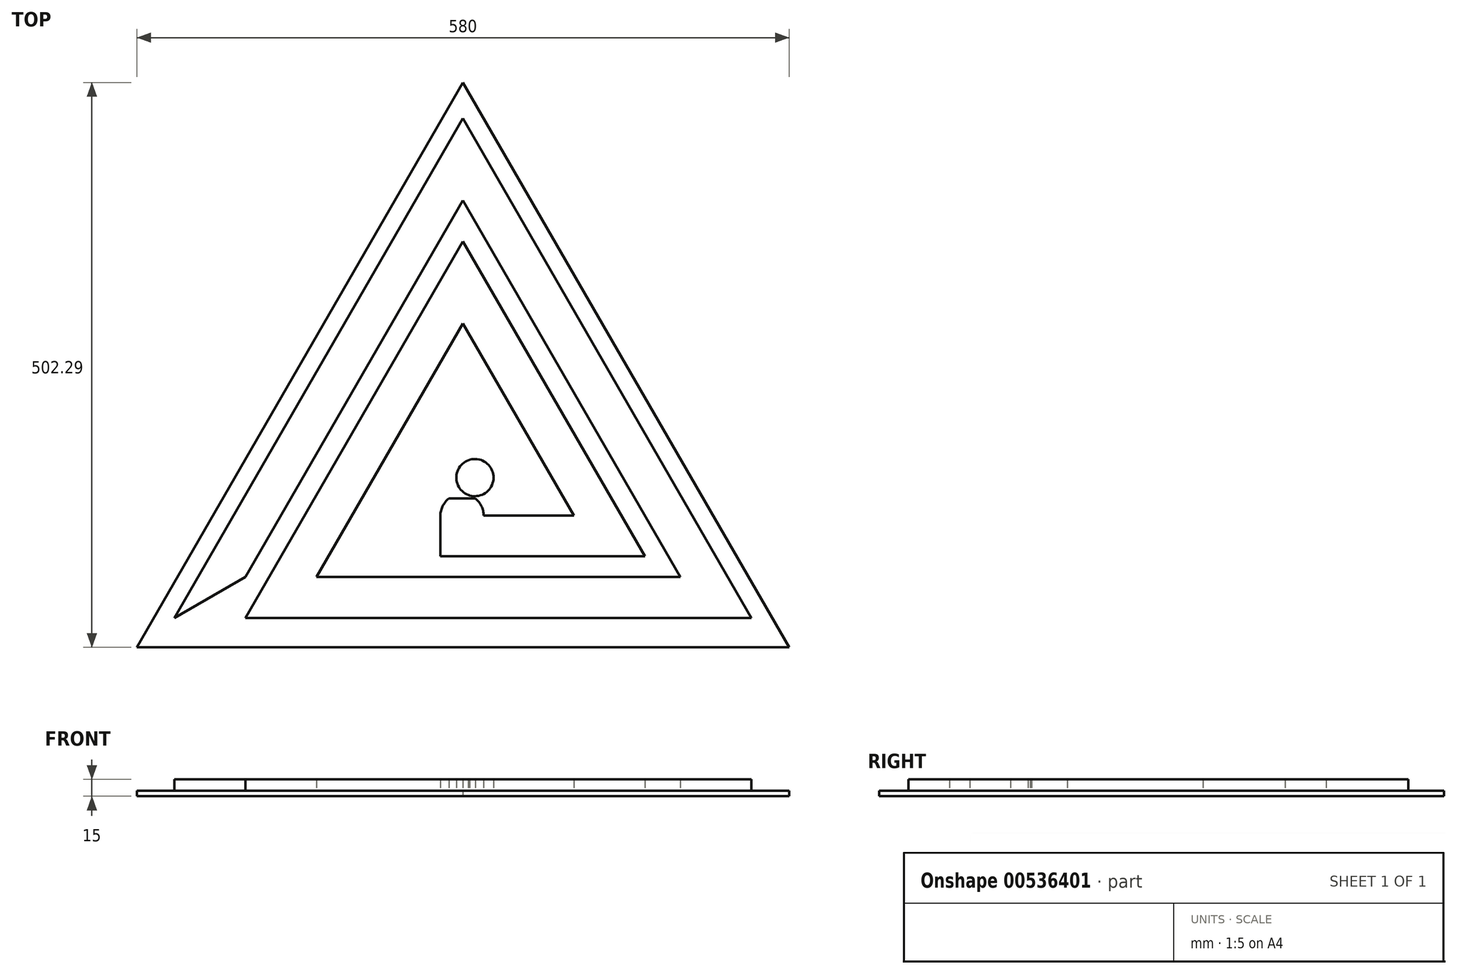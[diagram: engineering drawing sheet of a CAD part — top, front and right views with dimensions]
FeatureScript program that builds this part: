
annotation { "Feature Type Name" : "Feature", "Feature Type Description" : "" }
export const myFeature = defineFeature(function(context is Context, id is Id, definition is map)
    precondition{}
    {
        {
            var Q0;
            Q0=qCreatedBy(makeId("Top.planeOp"),FACE);
            var sketch = newSketch(context, id + "F0", { "sketchPlane" : qUnion([Q0])});
            skPoint(sketch, "E0.middle", {"position": v(0, 0) * mm});
            skLineSegment(sketch, "E1", {"start": v(499.99, -487.49) * mm, "end": v(499.99, -487.49) * mm});
            skLineSegment(sketch, "E2.0", {"start": v(0, 334.86) * mm, "end": v(290, -167.43) * mm});
            skLineSegment(sketch, "E2.1", {"start": v(290, -167.43) * mm, "end": v(-290, -167.43) * mm});
            skLineSegment(sketch, "E2.2", {"start": v(-290, -167.43) * mm, "end": v(0, 334.86) * mm});
            skSolve(sketch);
        }
        {
            var Q0;
            Q0=makeQuery(id+"F0.imprint","IMPRINT",FACE,{"disambiguationData":[TD([[makeQuery(id+"F0.imprint","IMPRINT",EDGE,{"derivedFrom":sQuery(id+"F0.wireOp",EDGE,"12a0643d-33db-4f89-9dce-d887bf9f58fb.0")}),-1.0]])]});
            var Q1;
            Q1=makeQuery(id+"F0.imprint","IMPRINT",FACE,{"disambiguationData":[TD([[makeQuery(id+"F0.imprint","IMPRINT",EDGE,{"derivedFrom":sQuery(id+"F0.wireOp",EDGE,"E2.0")}),-1.0]])]});
            extrude(context, id + "F1", {"entities" : qUnion([Q0, Q1]), "depth" : 5 * mm, "offsetDistance" : 25 * mm});
        }
        {
            var Q0;
            Q0=makeQuery(id+"F1.opExtrude","CAP_FACE",FACE,{"disambiguationData":[OSD([sQuery(id+"F0.wireOp",EDGE,"E2.0"),sQuery(id+"F0.wireOp",EDGE,"E2.1"),sQuery(id+"F0.wireOp",EDGE,"E2.2")])],"isStart":false});
            var sketch = newSketch(context, id + "F2", { "sketchPlane" : qUnion([Q0])});
            skLineSegment(sketch, "E3.0", {"start": v(-0.17, 303.1) * mm, "end": v(256.39, -141.27) * mm});
            skLineSegment(sketch, "E3.2", {"start": v(-256.73, -141.27) * mm, "end": v(-0.17, 303.1) * mm});
            skLineSegment(sketch, "E4", {"start": v(-193.55, -104.8) * mm, "end": v(-256.73, -141.27) * mm});
            skLineSegment(sketch, "E5.1", {"start": v(-193.55, -104.8) * mm, "end": v(-0.17, 230.14) * mm});
            skLineSegment(sketch, "E6", {"start": v(256.39, -141.27) * mm, "end": v(-193.55, -141.27) * mm});
            skLineSegment(sketch, "E7", {"start": v(-193.55, -141.27) * mm, "end": v(-0.17, 193.67) * mm});
            skLineSegment(sketch, "E8", {"start": v(-0.17, 193.67) * mm, "end": v(161.62, -86.56) * mm});
            skLineSegment(sketch, "E9", {"start": v(-0.17, 230.14) * mm, "end": v(193.2, -104.8) * mm});
            skLineSegment(sketch, "E10", {"start": v(193.2, -104.8) * mm, "end": v(-130.37, -104.8) * mm});
            skLineSegment(sketch, "E11", {"start": v(-130.37, -104.8) * mm, "end": v(-0.17, 120.71) * mm});
            skLineSegment(sketch, "E12", {"start": v(-0.17, 120.71) * mm, "end": v(98.61, -50.39) * mm});
            skLineSegment(sketch, "E13", {"start": v(98.61, -50.39) * mm, "end": v(18.38, -50.39) * mm});
            skLineSegment(sketch, "E14", {"start": v(-20.14, -86.56) * mm, "end": v(-20.14, -50.39) * mm});
            skLineSegment(sketch, "E15", {"start": v(-20.14, -86.56) * mm, "end": v(161.62, -86.56) * mm});
            skLineSegment(sketch, "E16.0", {"start": v(0, 70.2) * mm, "end": v(60.79, -35.1) * mm});
            skLineSegment(sketch, "E16.2", {"start": v(-61.13, -35.1) * mm, "end": v(0, 70.2) * mm});
            skPoint(sketch, "E17", {"position": v(10.83, -35.1) * mm});
            skPoint(sketch, "E18", {"position": v(10.6, -16.52) * mm});
            skLineSegment(sketch, "E19.2", {"start": v(-60.79, -35.1) * mm, "end": v(0, 70.2) * mm});
            skLineSegment(sketch, "E20", {"start": v(-60.79, -35.1) * mm, "end": v(60.79, -35.1) * mm});
            skArc(sketch, "E21", {"start": v(-20.14, -50.39) * mm, "mid": v(-0.88, -31.13) * mm, "end": v(18.38, -50.39) * mm});
            skArc(sketch, "E22", {"start": v(-0.88, -31.13) * mm, "mid": v(5.3, -32.15) * mm, "end": v(10.83, -35.1) * mm});
            skPoint(sketch, "E23", {"position": v(4.66, -31.94) * mm});
            skCircle(sketch, "E24", {"center": v(10.6, -16.52) * mm, "radius": 16.52 * mm});
            skSolve(sketch);
        }
        {
            var Q0;
            Q0=makeQuery(id+"F2.imprint","IMPRINT",FACE,{"disambiguationData":[TD([[makeQuery(id+"F2.imprint","IMPRINT",EDGE,{"derivedFrom":sQuery(id+"F2.wireOp",EDGE,"E3.2")}),-1.0]])]});
            extrude(context, id + "F3", {"entities" : qUnion([Q0]), "operationType" : NewBodyOperationType.ADD, "depth" : 10 * mm, "offsetDistance" : 25 * mm});
        }
        {
            var Q0;
            {var subQ1=sQuery(id+"F2.wireOp",EDGE,"E16.0");Q0=makeQuery(id+"F2.imprint","IMPRINT",FACE,{"disambiguationData":[TD([[makeQuery(id+"F2.imprint","IMPRINT",EDGE,{"derivedFrom":subQ1}),-1.0]])]});}
            var Q1;
            {var subQ0=sQuery(id+"F2.wireOp",EDGE,"E22");var subQ1=sQuery(id+"F2.wireOp",EDGE,"E21");var subQ6=makeQuery(id+"F2.imprint","INTERSECT",VERTEX,{"derivedFrom":[subQ1,subQ0]});Q1=makeQuery(id+"F2.imprint","IMPRINT",FACE,{"disambiguationData":[TD([[makeQuery(id+"F2.imprint","IMPRINT",EDGE,{"disambiguationData":[TD([[subQ6,1.0]])],"derivedFrom":subQ1}),-1.0]])]});}
            extrude(context, id + "F4", {"entities" : qUnion([Q0, Q1]), "operationType" : NewBodyOperationType.ADD, "depth" : 10 * mm, "offsetDistance" : 25 * mm});
        }
    });
